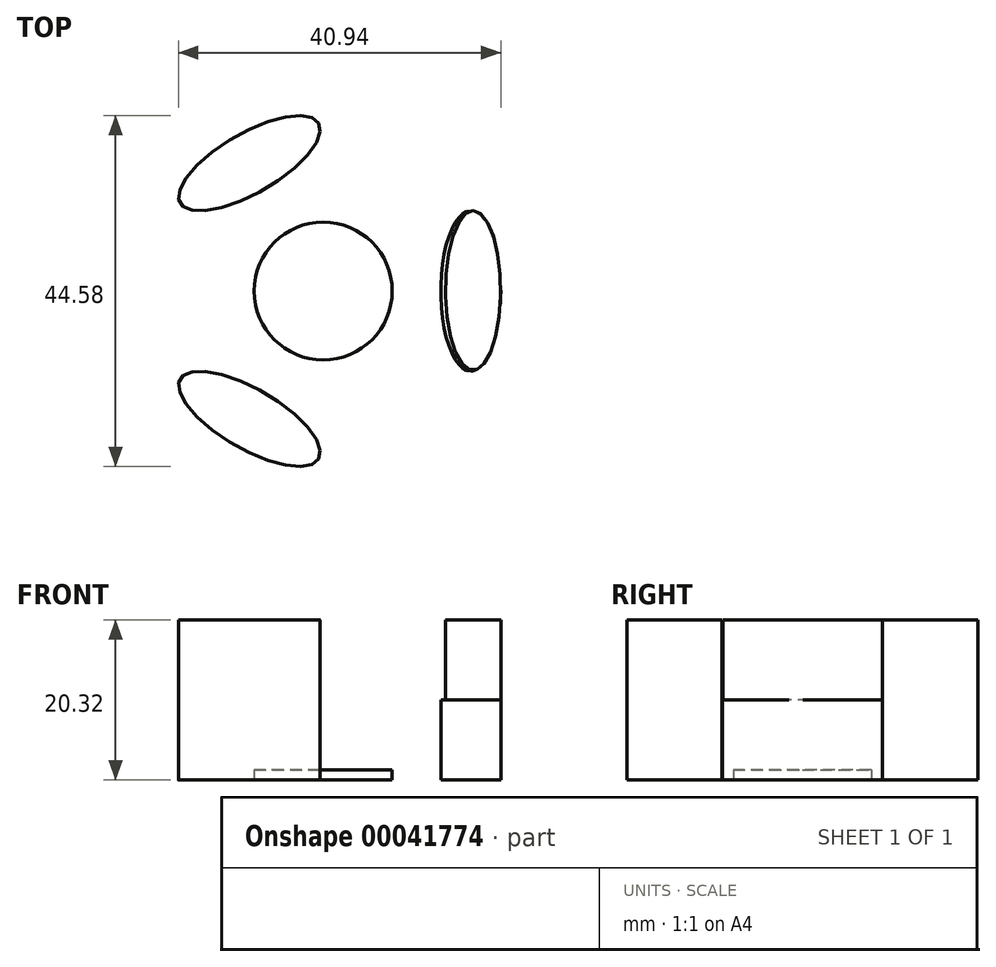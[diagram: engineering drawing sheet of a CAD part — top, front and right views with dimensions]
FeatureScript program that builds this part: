
annotation { "Feature Type Name" : "Feature", "Feature Type Description" : "" }
export const myFeature = defineFeature(function(context is Context, id is Id, definition is map)
    precondition{}
    {
        {
            var Q0;
            Q0=qCreatedBy(makeId("Top.planeOp"),FACE);
            var sketch = newSketch(context, id + "F0", { "sketchPlane" : qUnion([Q0])});
            skCircle(sketch, "E0", {"center": v(0, 0) * mm, "radius": 8.76 * mm});
            skEllipse(sketch, "E1", {"center": v(-18.75, 0) * mm, "majorRadius": 3.81 * mm, "minorRadius": 10.16 * mm, "majorAxis": v(1, 0)});
            skLineSegment(sketch, "E2", {"start": v(-8.76, 0) * mm, "end": v(-14.94, 0) * mm});
            skEllipse(sketch, "E3.1.0", {"center": v(-9.37, -16.23) * mm, "majorRadius": 3.81 * mm, "minorRadius": 10.16 * mm, "majorAxis": v(0.5, 0.87)});
            skEllipse(sketch, "E3.2.0", {"center": v(9.37, -16.23) * mm, "majorRadius": 3.81 * mm, "minorRadius": 10.16 * mm, "majorAxis": v(-0.5, 0.87)});
            skEllipse(sketch, "E3.3.0", {"center": v(18.75, 0) * mm, "majorRadius": 3.81 * mm, "minorRadius": 10.16 * mm, "majorAxis": v(-1, 0)});
            skEllipse(sketch, "E3.4.0", {"center": v(9.37, 16.23) * mm, "majorRadius": 3.81 * mm, "minorRadius": 10.16 * mm, "majorAxis": v(-0.5, -0.87)});
            skEllipse(sketch, "E3.5.0", {"center": v(-9.37, 16.23) * mm, "majorRadius": 3.81 * mm, "minorRadius": 10.16 * mm, "majorAxis": v(0.5, -0.87)});
            skFitSpline(sketch, "E4.0", {"points": [v(0.33, 21.17) * mm, v(0.1, 21.7) * mm, v(-0.25, 22.17) * mm, v(-0.7, 22.52) * mm, v(-1.22, 22.78) * mm, v(-1.8, 22.95) * mm, v(-2.43, 23.04) * mm, v(-3.35, 23.07) * mm, v(-4.6, 22.95) * mm, v(-6.25, 22.57) * mm, v(-8.04, 21.97) * mm, v(-9.55, 21.3) * mm, v(-10.76, 20.7) * mm, v(-11.66, 20.2) * mm, v(-12.54, 19.67) * mm, v(-13.68, 18.93) * mm, v(-15, 17.94) * mm, v(-16.42, 16.7) * mm, v(-17.58, 15.46) * mm, v(-18.3, 14.43) * mm, v(-18.74, 13.63) * mm, v(-18.97, 13.03) * mm, v(-19.12, 12.45) * mm, v(-19.16, 11.87) * mm, v(-19.07, 11.3) * mm, v(-18.85, 10.76) * mm, v(-18.5, 10.3) * mm, v(-18.05, 9.94) * mm, v(-17.52, 9.69) * mm, v(-16.94, 9.52) * mm, v(-16.31, 9.43) * mm, v(-15.4, 9.4) * mm, v(-14.15, 9.52) * mm, v(-12.5, 9.9) * mm, v(-10.7, 10.5) * mm, v(-9.2, 11.16) * mm, v(-7.98, 11.77) * mm, v(-7.08, 12.27) * mm, v(-6.2, 12.8) * mm, v(-5.07, 13.54) * mm, v(-3.74, 14.52) * mm, v(-2.33, 15.77) * mm, v(-1.17, 17.01) * mm, v(-0.44, 18.03) * mm, v(0, 18.84) * mm, v(0.23, 19.43) * mm, v(0.37, 20.02) * mm, v(0.41, 20.6) * mm, v(0.33, 21.17) * mm, v(0.1, 21.7) * mm, v(-0.25, 22.17) * mm, v(0.33, 21.17) * mm]});
            skFitSpline(sketch, "E5.0", {"points": [v(18.5, 10.3) * mm, v(18.85, 10.76) * mm, v(19.07, 11.3) * mm, v(19.16, 11.87) * mm, v(19.12, 12.45) * mm, v(18.97, 13.03) * mm, v(18.74, 13.63) * mm, v(18.3, 14.43) * mm, v(17.58, 15.46) * mm, v(16.42, 16.7) * mm, v(15, 17.94) * mm, v(13.68, 18.93) * mm, v(12.54, 19.67) * mm, v(11.66, 20.2) * mm, v(10.76, 20.7) * mm, v(9.55, 21.3) * mm, v(8.04, 21.97) * mm, v(6.25, 22.57) * mm, v(4.6, 22.95) * mm, v(3.35, 23.07) * mm, v(2.43, 23.04) * mm, v(1.8, 22.95) * mm, v(1.22, 22.78) * mm, v(0.7, 22.52) * mm, v(0.25, 22.17) * mm, v(-0.1, 21.7) * mm, v(-0.33, 21.17) * mm, v(-0.41, 20.6) * mm, v(-0.37, 20.02) * mm, v(-0.23, 19.43) * mm, v(0, 18.84) * mm, v(0.44, 18.03) * mm, v(1.17, 17.01) * mm, v(2.33, 15.77) * mm, v(3.74, 14.52) * mm, v(5.07, 13.54) * mm, v(6.2, 12.8) * mm, v(7.08, 12.27) * mm, v(7.98, 11.77) * mm, v(9.2, 11.16) * mm, v(10.7, 10.5) * mm, v(12.5, 9.9) * mm, v(14.15, 9.52) * mm, v(15.4, 9.4) * mm, v(16.31, 9.43) * mm, v(16.94, 9.52) * mm, v(17.52, 9.69) * mm, v(18.05, 9.94) * mm, v(18.5, 10.3) * mm, v(18.85, 10.76) * mm, v(19.07, 11.3) * mm, v(18.5, 10.3) * mm]});
            skFitSpline(sketch, "E6.0", {"points": [v(18.17, -10.87) * mm, v(18.75, -10.95) * mm, v(19.32, -10.87) * mm, v(19.86, -10.66) * mm, v(20.34, -10.33) * mm, v(20.77, -9.91) * mm, v(21.17, -9.41) * mm, v(21.65, -8.64) * mm, v(22.17, -7.5) * mm, v(22.67, -5.87) * mm, v(23.04, -4.02) * mm, v(23.23, -2.38) * mm, v(23.3, -1.03) * mm, v(23.32, 0) * mm, v(23.3, 1.03) * mm, v(23.23, 2.38) * mm, v(23.04, 4.02) * mm, v(22.67, 5.87) * mm, v(22.17, 7.5) * mm, v(21.65, 8.64) * mm, v(21.17, 9.41) * mm, v(20.77, 9.91) * mm, v(20.34, 10.33) * mm, v(19.86, 10.66) * mm, v(19.32, 10.87) * mm, v(18.75, 10.95) * mm, v(18.17, 10.87) * mm, v(17.64, 10.66) * mm, v(17.15, 10.33) * mm, v(16.72, 9.91) * mm, v(16.32, 9.41) * mm, v(15.84, 8.64) * mm, v(15.32, 7.5) * mm, v(14.82, 5.87) * mm, v(14.45, 4.02) * mm, v(14.26, 2.38) * mm, v(14.19, 1.03) * mm, v(14.17, 0) * mm, v(14.19, -1.03) * mm, v(14.26, -2.38) * mm, v(14.45, -4.02) * mm, v(14.82, -5.87) * mm, v(15.32, -7.5) * mm, v(15.84, -8.64) * mm, v(16.32, -9.41) * mm, v(16.72, -9.91) * mm, v(17.15, -10.33) * mm, v(17.64, -10.66) * mm, v(18.17, -10.87) * mm, v(18.75, -10.95) * mm, v(19.32, -10.87) * mm, v(18.17, -10.87) * mm]});
            skFitSpline(sketch, "E7.0", {"points": [v(-0.33, -21.17) * mm, v(-0.1, -21.7) * mm, v(0.25, -22.17) * mm, v(0.7, -22.52) * mm, v(1.22, -22.78) * mm, v(1.8, -22.95) * mm, v(2.43, -23.04) * mm, v(3.35, -23.07) * mm, v(4.6, -22.95) * mm, v(6.25, -22.57) * mm, v(8.04, -21.97) * mm, v(9.55, -21.3) * mm, v(10.76, -20.7) * mm, v(11.66, -20.2) * mm, v(12.54, -19.67) * mm, v(13.68, -18.93) * mm, v(15, -17.94) * mm, v(16.42, -16.7) * mm, v(17.58, -15.46) * mm, v(18.3, -14.43) * mm, v(18.74, -13.63) * mm, v(18.97, -13.03) * mm, v(19.12, -12.45) * mm, v(19.16, -11.87) * mm, v(19.07, -11.3) * mm, v(18.85, -10.76) * mm, v(18.5, -10.3) * mm, v(18.05, -9.94) * mm, v(17.52, -9.69) * mm, v(16.94, -9.52) * mm, v(16.31, -9.43) * mm, v(15.4, -9.4) * mm, v(14.15, -9.52) * mm, v(12.5, -9.9) * mm, v(10.7, -10.5) * mm, v(9.2, -11.16) * mm, v(7.98, -11.77) * mm, v(7.08, -12.27) * mm, v(6.2, -12.8) * mm, v(5.07, -13.54) * mm, v(3.74, -14.52) * mm, v(2.33, -15.77) * mm, v(1.17, -17.01) * mm, v(0.44, -18.03) * mm, v(0, -18.84) * mm, v(-0.23, -19.43) * mm, v(-0.37, -20.02) * mm, v(-0.41, -20.6) * mm, v(-0.33, -21.17) * mm, v(-0.1, -21.7) * mm, v(0.25, -22.17) * mm, v(-0.33, -21.17) * mm]});
            skFitSpline(sketch, "E8.0", {"points": [v(-18.17, 10.87) * mm, v(-18.75, 10.95) * mm, v(-19.32, 10.87) * mm, v(-19.86, 10.66) * mm, v(-20.34, 10.33) * mm, v(-20.77, 9.91) * mm, v(-21.17, 9.41) * mm, v(-21.65, 8.64) * mm, v(-22.17, 7.5) * mm, v(-22.67, 5.87) * mm, v(-23.04, 4.02) * mm, v(-23.23, 2.38) * mm, v(-23.3, 1.03) * mm, v(-23.32, 0) * mm, v(-23.3, -1.03) * mm, v(-23.23, -2.38) * mm, v(-23.04, -4.02) * mm, v(-22.67, -5.87) * mm, v(-22.17, -7.5) * mm, v(-21.65, -8.64) * mm, v(-21.17, -9.41) * mm, v(-20.77, -9.91) * mm, v(-20.34, -10.33) * mm, v(-19.86, -10.66) * mm, v(-19.32, -10.87) * mm, v(-18.75, -10.95) * mm, v(-18.17, -10.87) * mm, v(-17.64, -10.66) * mm, v(-17.15, -10.33) * mm, v(-16.72, -9.91) * mm, v(-16.32, -9.41) * mm, v(-15.84, -8.64) * mm, v(-15.32, -7.5) * mm, v(-14.82, -5.87) * mm, v(-14.45, -4.02) * mm, v(-14.26, -2.38) * mm, v(-14.19, -1.03) * mm, v(-14.17, 0) * mm, v(-14.19, 1.03) * mm, v(-14.26, 2.38) * mm, v(-14.45, 4.02) * mm, v(-14.82, 5.87) * mm, v(-15.32, 7.5) * mm, v(-15.84, 8.64) * mm, v(-16.32, 9.41) * mm, v(-16.72, 9.91) * mm, v(-17.15, 10.33) * mm, v(-17.64, 10.66) * mm, v(-18.17, 10.87) * mm, v(-18.75, 10.95) * mm, v(-19.32, 10.87) * mm, v(-18.17, 10.87) * mm]});
            skFitSpline(sketch, "E9.0", {"points": [v(-18.5, -10.3) * mm, v(-18.85, -10.76) * mm, v(-19.07, -11.3) * mm, v(-19.16, -11.87) * mm, v(-19.12, -12.45) * mm, v(-18.97, -13.03) * mm, v(-18.74, -13.63) * mm, v(-18.3, -14.43) * mm, v(-17.58, -15.46) * mm, v(-16.42, -16.7) * mm, v(-15, -17.94) * mm, v(-13.68, -18.93) * mm, v(-12.54, -19.67) * mm, v(-11.66, -20.2) * mm, v(-10.76, -20.7) * mm, v(-9.55, -21.3) * mm, v(-8.04, -21.97) * mm, v(-6.25, -22.57) * mm, v(-4.6, -22.95) * mm, v(-3.35, -23.07) * mm, v(-2.43, -23.04) * mm, v(-1.8, -22.95) * mm, v(-1.22, -22.78) * mm, v(-0.7, -22.52) * mm, v(-0.25, -22.17) * mm, v(0.1, -21.7) * mm, v(0.33, -21.17) * mm, v(0.41, -20.6) * mm, v(0.37, -20.02) * mm, v(0.23, -19.43) * mm, v(0, -18.84) * mm, v(-0.44, -18.03) * mm, v(-1.17, -17.01) * mm, v(-2.33, -15.77) * mm, v(-3.74, -14.52) * mm, v(-5.07, -13.54) * mm, v(-6.2, -12.8) * mm, v(-7.08, -12.27) * mm, v(-7.98, -11.77) * mm, v(-9.2, -11.16) * mm, v(-10.7, -10.5) * mm, v(-12.5, -9.9) * mm, v(-14.15, -9.52) * mm, v(-15.4, -9.4) * mm, v(-16.31, -9.43) * mm, v(-16.94, -9.52) * mm, v(-17.52, -9.69) * mm, v(-18.05, -9.94) * mm, v(-18.5, -10.3) * mm, v(-18.85, -10.76) * mm, v(-19.07, -11.3) * mm, v(-18.5, -10.3) * mm]});
            skFitSpline(sketch, "E10.0", {"points": [v(-0.04, 21.07) * mm, v(-0.23, 21.51) * mm, v(-0.52, 21.9) * mm, v(-1.03, 22.3) * mm, v(-1.85, 22.6) * mm, v(-3.09, 22.71) * mm, v(-4.53, 22.57) * mm, v(-6.15, 22.2) * mm, v(-7.9, 21.61) * mm, v(-9.4, 20.96) * mm, v(-10.58, 20.36) * mm, v(-11.47, 19.87) * mm, v(-12.34, 19.34) * mm, v(-13.46, 18.61) * mm, v(-14.77, 17.65) * mm, v(-16.15, 16.43) * mm, v(-17.28, 15.21) * mm, v(-18.13, 14.03) * mm, v(-18.65, 12.9) * mm, v(-18.8, 12.04) * mm, v(-18.7, 11.4) * mm, v(-18.52, 10.95) * mm, v(-18.23, 10.57) * mm, v(-17.72, 10.17) * mm, v(-16.9, 9.86) * mm, v(-15.66, 9.75) * mm, v(-14.21, 9.9) * mm, v(-12.6, 10.26) * mm, v(-10.85, 10.86) * mm, v(-9.35, 11.5) * mm, v(-8.16, 12.1) * mm, v(-7.27, 12.6) * mm, v(-6.4, 13.12) * mm, v(-5.29, 13.85) * mm, v(-3.98, 14.82) * mm, v(-2.6, 16.04) * mm, v(-1.46, 17.26) * mm, v(-0.62, 18.44) * mm, v(-0.1, 19.56) * mm, v(0.05, 20.43) * mm, v(-0.04, 21.07) * mm, v(-0.23, 21.51) * mm, v(-0.52, 21.9) * mm, v(-0.04, 21.07) * mm]});
            skFitSpline(sketch, "E11.0", {"points": [v(-18.27, 10.5) * mm, v(-18.75, 10.56) * mm, v(-19.22, 10.5) * mm, v(-19.82, 10.26) * mm, v(-20.5, 9.7) * mm, v(-21.21, 8.68) * mm, v(-21.81, 7.36) * mm, v(-22.3, 5.78) * mm, v(-22.67, 3.97) * mm, v(-22.85, 2.35) * mm, v(-22.92, 1.02) * mm, v(-22.94, 0) * mm, v(-22.92, -1.02) * mm, v(-22.85, -2.35) * mm, v(-22.67, -3.97) * mm, v(-22.3, -5.78) * mm, v(-21.81, -7.36) * mm, v(-21.21, -8.68) * mm, v(-20.5, -9.7) * mm, v(-19.82, -10.26) * mm, v(-19.22, -10.5) * mm, v(-18.75, -10.56) * mm, v(-18.27, -10.5) * mm, v(-17.67, -10.26) * mm, v(-16.99, -9.7) * mm, v(-16.28, -8.68) * mm, v(-15.68, -7.36) * mm, v(-15.19, -5.78) * mm, v(-14.82, -3.97) * mm, v(-14.64, -2.35) * mm, v(-14.57, -1.02) * mm, v(-14.55, 0) * mm, v(-14.57, 1.02) * mm, v(-14.64, 2.35) * mm, v(-14.82, 3.97) * mm, v(-15.19, 5.78) * mm, v(-15.68, 7.36) * mm, v(-16.28, 8.68) * mm, v(-16.99, 9.7) * mm, v(-17.67, 10.26) * mm, v(-18.27, 10.5) * mm, v(-18.75, 10.56) * mm, v(-19.22, 10.5) * mm, v(-18.27, 10.5) * mm]});
            skFitSpline(sketch, "E12.0", {"points": [v(-18.23, -10.57) * mm, v(-18.52, -10.95) * mm, v(-18.7, -11.4) * mm, v(-18.8, -12.04) * mm, v(-18.65, -12.9) * mm, v(-18.13, -14.03) * mm, v(-17.28, -15.21) * mm, v(-16.15, -16.43) * mm, v(-14.77, -17.65) * mm, v(-13.46, -18.61) * mm, v(-12.34, -19.34) * mm, v(-11.47, -19.87) * mm, v(-10.58, -20.36) * mm, v(-9.4, -20.96) * mm, v(-7.9, -21.61) * mm, v(-6.15, -22.2) * mm, v(-4.53, -22.57) * mm, v(-3.09, -22.71) * mm, v(-1.85, -22.6) * mm, v(-1.03, -22.3) * mm, v(-0.52, -21.9) * mm, v(-0.23, -21.51) * mm, v(-0.04, -21.07) * mm, v(0.05, -20.43) * mm, v(-0.1, -19.56) * mm, v(-0.62, -18.44) * mm, v(-1.46, -17.26) * mm, v(-2.6, -16.04) * mm, v(-3.98, -14.82) * mm, v(-5.29, -13.85) * mm, v(-6.4, -13.12) * mm, v(-7.27, -12.6) * mm, v(-8.16, -12.1) * mm, v(-9.35, -11.5) * mm, v(-10.85, -10.86) * mm, v(-12.6, -10.26) * mm, v(-14.21, -9.9) * mm, v(-15.66, -9.75) * mm, v(-16.9, -9.86) * mm, v(-17.72, -10.17) * mm, v(-18.23, -10.57) * mm, v(-18.52, -10.95) * mm, v(-18.7, -11.4) * mm, v(-18.23, -10.57) * mm]});
            skFitSpline(sketch, "E13.0", {"points": [v(0.04, -21.07) * mm, v(0.23, -21.51) * mm, v(0.52, -21.9) * mm, v(1.03, -22.3) * mm, v(1.85, -22.6) * mm, v(3.09, -22.71) * mm, v(4.53, -22.57) * mm, v(6.15, -22.2) * mm, v(7.9, -21.61) * mm, v(9.4, -20.96) * mm, v(10.58, -20.36) * mm, v(11.47, -19.87) * mm, v(12.34, -19.34) * mm, v(13.46, -18.61) * mm, v(14.77, -17.65) * mm, v(16.15, -16.43) * mm, v(17.28, -15.21) * mm, v(18.13, -14.03) * mm, v(18.65, -12.9) * mm, v(18.8, -12.04) * mm, v(18.7, -11.4) * mm, v(18.52, -10.95) * mm, v(18.23, -10.57) * mm, v(17.72, -10.17) * mm, v(16.9, -9.86) * mm, v(15.66, -9.75) * mm, v(14.21, -9.9) * mm, v(12.6, -10.26) * mm, v(10.85, -10.86) * mm, v(9.35, -11.5) * mm, v(8.16, -12.1) * mm, v(7.27, -12.6) * mm, v(6.4, -13.12) * mm, v(5.29, -13.85) * mm, v(3.98, -14.82) * mm, v(2.6, -16.04) * mm, v(1.46, -17.26) * mm, v(0.62, -18.44) * mm, v(0.1, -19.56) * mm, v(-0.05, -20.43) * mm, v(0.04, -21.07) * mm, v(0.23, -21.51) * mm, v(0.52, -21.9) * mm, v(0.04, -21.07) * mm]});
            skFitSpline(sketch, "E14.0", {"points": [v(18.27, -10.5) * mm, v(18.75, -10.56) * mm, v(19.22, -10.5) * mm, v(19.82, -10.26) * mm, v(20.5, -9.7) * mm, v(21.21, -8.68) * mm, v(21.81, -7.36) * mm, v(22.3, -5.78) * mm, v(22.67, -3.97) * mm, v(22.85, -2.35) * mm, v(22.92, -1.02) * mm, v(22.94, 0) * mm, v(22.92, 1.02) * mm, v(22.85, 2.35) * mm, v(22.67, 3.97) * mm, v(22.3, 5.78) * mm, v(21.81, 7.36) * mm, v(21.21, 8.68) * mm, v(20.5, 9.7) * mm, v(19.82, 10.26) * mm, v(19.22, 10.5) * mm, v(18.75, 10.56) * mm, v(18.27, 10.5) * mm, v(17.67, 10.26) * mm, v(16.99, 9.7) * mm, v(16.28, 8.68) * mm, v(15.68, 7.36) * mm, v(15.19, 5.78) * mm, v(14.82, 3.97) * mm, v(14.64, 2.35) * mm, v(14.57, 1.02) * mm, v(14.55, 0) * mm, v(14.57, -1.02) * mm, v(14.64, -2.35) * mm, v(14.82, -3.97) * mm, v(15.19, -5.78) * mm, v(15.68, -7.36) * mm, v(16.28, -8.68) * mm, v(16.99, -9.7) * mm, v(17.67, -10.26) * mm, v(18.27, -10.5) * mm, v(18.75, -10.56) * mm, v(19.22, -10.5) * mm, v(18.27, -10.5) * mm]});
            skFitSpline(sketch, "E15.0", {"points": [v(18.23, 10.57) * mm, v(18.52, 10.95) * mm, v(18.7, 11.4) * mm, v(18.8, 12.04) * mm, v(18.65, 12.9) * mm, v(18.13, 14.03) * mm, v(17.28, 15.21) * mm, v(16.15, 16.43) * mm, v(14.77, 17.65) * mm, v(13.46, 18.61) * mm, v(12.34, 19.34) * mm, v(11.47, 19.87) * mm, v(10.58, 20.36) * mm, v(9.4, 20.96) * mm, v(7.9, 21.61) * mm, v(6.15, 22.2) * mm, v(4.53, 22.57) * mm, v(3.09, 22.71) * mm, v(1.85, 22.6) * mm, v(1.03, 22.3) * mm, v(0.52, 21.9) * mm, v(0.23, 21.51) * mm, v(0.04, 21.07) * mm, v(-0.05, 20.43) * mm, v(0.1, 19.56) * mm, v(0.62, 18.44) * mm, v(1.46, 17.26) * mm, v(2.6, 16.04) * mm, v(3.98, 14.82) * mm, v(5.29, 13.85) * mm, v(6.4, 13.12) * mm, v(7.27, 12.6) * mm, v(8.16, 12.1) * mm, v(9.35, 11.5) * mm, v(10.85, 10.86) * mm, v(12.6, 10.26) * mm, v(14.21, 9.9) * mm, v(15.66, 9.75) * mm, v(16.9, 9.86) * mm, v(17.72, 10.17) * mm, v(18.23, 10.57) * mm, v(18.52, 10.95) * mm, v(18.7, 11.4) * mm, v(18.23, 10.57) * mm]});
            skSolve(sketch);
        }
        {
            var Q0;
            {var subQ0=sQuery(id+"F0.wireOp",EDGE,"E8.0");var subQ1=sQuery(id+"F0.wireOp",EDGE,"E3.5.0");var subQ3=makeQuery(id+"F0.imprint","INTERSECT",VERTEX,{"disambiguationData":[OD(0.0)],"derivedFrom":[subQ1,subQ0]});Q0=makeQuery(id+"F0.imprint","IMPRINT",FACE,{"disambiguationData":[TD([[makeQuery(id+"F0.imprint","IMPRINT",EDGE,{"disambiguationData":[TD([[subQ3,-1.0]])],"derivedFrom":subQ1}),1.0]])]});}
            var Q1;
            {var subQ0=sQuery(id+"F0.wireOp",EDGE,"E8.0");var subQ3=sQuery(id+"F0.wireOp",EDGE,"E3.5.0");var subQ4=makeQuery(id+"F0.imprint","INTERSECT",VERTEX,{"disambiguationData":[OD(0.0)],"derivedFrom":[subQ3,subQ0]});Q1=makeQuery(id+"F0.imprint","IMPRINT",FACE,{"disambiguationData":[TD([[makeQuery(id+"F0.imprint","IMPRINT",EDGE,{"disambiguationData":[TD([[subQ4,-1.0]])],"derivedFrom":subQ3}),-1.0]])]});}
            var Q2;
            Q2=makeQuery(id+"F0.imprint","IMPRINT",FACE,{"disambiguationData":[TD([[makeQuery(id+"F0.imprint","IMPRINT",EDGE,{"derivedFrom":sQuery(id+"F0.wireOp",EDGE,"E0")}),-1.0]])]});
            var Q3;
            {var subQ0=sQuery(id+"F0.wireOp",EDGE,"E8.0");var subQ3=sQuery(id+"F0.wireOp",EDGE,"E4.0");var subQ4=makeQuery(id+"F0.imprint","INTERSECT",VERTEX,{"disambiguationData":[OD(1.0)],"derivedFrom":[subQ3,subQ0]});Q3=makeQuery(id+"F0.imprint","IMPRINT",FACE,{"disambiguationData":[TD([[makeQuery(id+"F0.imprint","IMPRINT",EDGE,{"disambiguationData":[TD([[subQ4,-1.0]])],"derivedFrom":subQ3}),1.0]])]});}
            var Q4;
            {var subQ1=sQuery(id+"F0.wireOp",EDGE,"E3.3.0");var subQ4=sQuery(id+"F0.wireOp",EDGE,"E5.0");var subQ6=makeQuery(id+"F0.imprint","INTERSECT",VERTEX,{"disambiguationData":[OD(0.0)],"derivedFrom":[subQ1,subQ4]});Q4=makeQuery(id+"F0.imprint","IMPRINT",FACE,{"disambiguationData":[TD([[makeQuery(id+"F0.imprint","IMPRINT",EDGE,{"disambiguationData":[TD([[subQ6,-1.0]])],"derivedFrom":subQ1}),1.0]])]});}
            var Q5;
            {var subQ3=sQuery(id+"F0.wireOp",EDGE,"E5.0");var subQ5=sQuery(id+"F0.wireOp",EDGE,"E3.3.0");var subQ7=makeQuery(id+"F0.imprint","INTERSECT",VERTEX,{"disambiguationData":[OD(0.0)],"derivedFrom":[subQ5,subQ3]});Q5=makeQuery(id+"F0.imprint","IMPRINT",FACE,{"disambiguationData":[TD([[makeQuery(id+"F0.imprint","IMPRINT",EDGE,{"disambiguationData":[TD([[subQ7,-1.0]])],"derivedFrom":subQ5}),-1.0]])]});}
            var Q6;
            {var subQ3=sQuery(id+"F0.wireOp",EDGE,"E6.0");var subQ5=sQuery(id+"F0.wireOp",EDGE,"E5.0");var subQ6=makeQuery(id+"F0.imprint","INTERSECT",VERTEX,{"disambiguationData":[OD(1.0)],"derivedFrom":[subQ5,subQ3]});Q6=makeQuery(id+"F0.imprint","IMPRINT",FACE,{"disambiguationData":[TD([[makeQuery(id+"F0.imprint","IMPRINT",EDGE,{"disambiguationData":[TD([[subQ6,-1.0]])],"derivedFrom":subQ5}),-1.0]])]});}
            var Q7;
            {var subQ3=sQuery(id+"F0.wireOp",EDGE,"E7.0");var subQ5=sQuery(id+"F0.wireOp",EDGE,"E9.0");var subQ7=makeQuery(id+"F0.imprint","INTERSECT",VERTEX,{"disambiguationData":[OD(1.0)],"derivedFrom":[subQ3,subQ5]});Q7=makeQuery(id+"F0.imprint","IMPRINT",FACE,{"disambiguationData":[TD([[makeQuery(id+"F0.imprint","IMPRINT",EDGE,{"disambiguationData":[TD([[subQ7,-1.0]])],"derivedFrom":subQ3}),-1.0]])]});}
            var Q8;
            {var subQ3=sQuery(id+"F0.wireOp",EDGE,"E7.0");var subQ5=sQuery(id+"F0.wireOp",EDGE,"E3.1.0");var subQ7=makeQuery(id+"F0.imprint","INTERSECT",VERTEX,{"disambiguationData":[OD(0.0)],"derivedFrom":[subQ5,subQ3]});Q8=makeQuery(id+"F0.imprint","IMPRINT",FACE,{"disambiguationData":[TD([[makeQuery(id+"F0.imprint","IMPRINT",EDGE,{"disambiguationData":[TD([[subQ7,-1.0]])],"derivedFrom":subQ5}),-1.0]])]});}
            var Q9;
            {var subQ1=sQuery(id+"F0.wireOp",EDGE,"E3.1.0");var subQ4=sQuery(id+"F0.wireOp",EDGE,"E7.0");var subQ6=makeQuery(id+"F0.imprint","INTERSECT",VERTEX,{"disambiguationData":[OD(0.0)],"derivedFrom":[subQ1,subQ4]});Q9=makeQuery(id+"F0.imprint","IMPRINT",FACE,{"disambiguationData":[TD([[makeQuery(id+"F0.imprint","IMPRINT",EDGE,{"disambiguationData":[TD([[subQ6,-1.0]])],"derivedFrom":subQ1}),1.0]])]});}
            var Q10;
            Q10=makeQuery(id+"F0.imprint","IMPRINT",FACE,{"disambiguationData":[TD([[makeQuery(id+"F0.imprint","IMPRINT",EDGE,{"derivedFrom":sQuery(id+"F0.wireOp",EDGE,"E0")}),1.0]])]});
            extrude(context, id + "F1", {"entities" : qUnion([Q0, Q1, Q2, Q3, Q4, Q5, Q6, Q7, Q8, Q9, Q10]), "depth" : 10.16 * mm});
        }
        {
            var Q0;
            Q0=makeQuery(id+"F1.opExtrude","CAP_FACE",FACE,{"disambiguationData":[OSD([sQuery(id+"F0.wireOp",EDGE,"E0"),sQuery(id+"F0.wireOp",EDGE,"E3.1.0"),sQuery(id+"F0.wireOp",EDGE,"E3.3.0"),sQuery(id+"F0.wireOp",EDGE,"E3.5.0"),sQuery(id+"F0.wireOp",EDGE,"E5.0"),sQuery(id+"F0.wireOp",EDGE,"E7.0"),sQuery(id+"F0.wireOp",EDGE,"E8.0")])],"isStart":false});
            var sketch = newSketch(context, id + "F2", { "sketchPlane" : qUnion([Q0])});
            skEllipse(sketch, "E16", {"center": v(-9.37, -16.23) * mm, "majorRadius": 3.81 * mm, "minorRadius": 10.16 * mm, "majorAxis": v(-0.5, -0.87)});
            skEllipse(sketch, "E17", {"center": v(19.05, 0.06) * mm, "majorRadius": 3.5 * mm, "minorRadius": 10.13 * mm, "majorAxis": v(1, 0)});
            skEllipse(sketch, "E18", {"center": v(-9.37, 16.23) * mm, "majorRadius": 10.16 * mm, "minorRadius": 3.81 * mm, "majorAxis": v(0.87, 0.5)});
            skSolve(sketch);
        }
        {
            var Q0;
            {var subQ0=makeQuery(id+"F1.opExtrude","CAP_EDGE",EDGE,{"disambiguationData":[OSD([sQuery(id+"F0.wireOp",EDGE,"E8.0")])],"isStart":false});var subQ1=sQuery(id+"F2.wireOp",EDGE,"E18");var subQ2=makeQuery(id+"F2.imprint","INTERSECT",VERTEX,{"disambiguationData":[OD(1.0)],"derivedFrom":[subQ0,subQ1]});Q0=makeQuery(id+"F2.imprint","IMPRINT",FACE,{"disambiguationData":[TD([[makeQuery(id+"F2.imprint","IMPRINT",EDGE,{"disambiguationData":[TD([[subQ2,-1.0]])],"derivedFrom":subQ1}),1.0]])]});}
            var Q1;
            {var subQ1=sQuery(id+"F2.wireOp",EDGE,"E16");var subQ4=makeQuery(id+"F1.opExtrude","CAP_EDGE",EDGE,{"disambiguationData":[OSD([sQuery(id+"F0.wireOp",EDGE,"E7.0")])],"isStart":false});var subQ5=makeQuery(id+"F2.imprint","INTERSECT",VERTEX,{"disambiguationData":[OD(1.0)],"derivedFrom":[subQ4,subQ1]});Q1=makeQuery(id+"F2.imprint","IMPRINT",FACE,{"disambiguationData":[TD([[makeQuery(id+"F2.imprint","IMPRINT",EDGE,{"disambiguationData":[TD([[subQ5,-1.0]])],"derivedFrom":subQ1}),1.0]])]});}
            var Q2;
            {var subQ0=makeQuery(id+"F1.opExtrude","CAP_EDGE",EDGE,{"disambiguationData":[OSD([sQuery(id+"F0.wireOp",EDGE,"E3.3.0")])],"isStart":false});var subQ1=sQuery(id+"F2.wireOp",EDGE,"E17");var subQ5=makeQuery(id+"F2.imprint","INTERSECT",VERTEX,{"disambiguationData":[OD(0.0)],"derivedFrom":[subQ0,subQ1]});Q2=makeQuery(id+"F2.imprint","IMPRINT",FACE,{"disambiguationData":[TD([[makeQuery(id+"F2.imprint","IMPRINT",EDGE,{"disambiguationData":[TD([[subQ5,1.0]])],"derivedFrom":subQ1}),1.0]])]});}
            extrude(context, id + "F3", {"entities" : qUnion([Q0, Q1, Q2]), "operationType" : NewBodyOperationType.ADD, "depth" : 10.16 * mm});
        }
        {
            var Q0;
            Q0=makeQuery(id+"F1.opExtrude","CAP_FACE",FACE,{"disambiguationData":[OSD([sQuery(id+"F0.wireOp",EDGE,"E3.1.0"),sQuery(id+"F0.wireOp",EDGE,"E3.3.0"),sQuery(id+"F0.wireOp",EDGE,"E3.5.0"),sQuery(id+"F0.wireOp",EDGE,"E5.0"),sQuery(id+"F0.wireOp",EDGE,"E7.0"),sQuery(id+"F0.wireOp",EDGE,"E8.0")])],"isStart":false});
            var sketch = newSketch(context, id + "F4", { "sketchPlane" : qUnion([Q0])});
            skCircle(sketch, "E19", {"center": v(0, 0) * mm, "radius": 9.53 * mm});
            skPoint(sketch, "E20.start.orphan", {"position": v(-14.17, 0) * mm});
            skSolve(sketch);
        }
        {
            var Q0;
            Q0=makeQuery(id+"F4.imprint","IMPRINT",FACE,{"disambiguationData":[TD([[makeQuery(id+"F4.imprint","IMPRINT",EDGE,{"derivedFrom":sQuery(id+"F4.wireOp",EDGE,"E19")}),1.0]])]});
            extrude(context, id + "F5", {"entities" : qUnion([Q0]), "operationType" : NewBodyOperationType.REMOVE, "oppositeDirection" : true, "depth" : 8.9 * mm});
        }
    });
